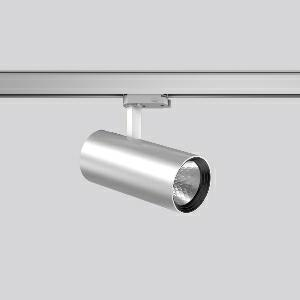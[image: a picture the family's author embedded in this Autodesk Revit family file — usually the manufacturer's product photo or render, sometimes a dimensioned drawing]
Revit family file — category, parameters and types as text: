
# Revit family: deecos_s_mini_742204_004_76_07a7
name_source: partatom
category: Lighting Fixtures
units: mm (PartAtom-declared; Revit-internal decimal feet)

## family parameters
Cut with Voids When Loaded = No
Host = Face
Light Source = No
Part Type = Normal
Room Calculation Point = No
Round Connector Dimension = Use Diameter
Shared = No

## types (1)
- DEECOS S mini (1 x LED Modul 930, 3500 lm, 3000)
    Apparent Load = 29 VA
    Approval mark = CE
    CIE Flux Codes = 99 100 100 100 100
    Color Rendering = 90
    Color Temperature = 3000
    Default Elevation = 1800 mm
    Description = Series: DEECOS S mini
LED surface-mounted projector in modern design with no visible cooling ribs. Housing: die-cast aluminium, powder-coated. Rotation range: 356°. Swivel range: 90°. Black plastic ring and recessed LED to prevent glare from the side. Optical assembly with reflector made of MIRO-Silver with 98% total light reflection for outstanding efficiency - can be changed without tools. Best colour rendering index Ra>90. With adapter for RZB 3-circuit DALI tracks. Suitable for Track on ceiling, Wall track. High quality converter without flickering and stroboscopic effect. The following accessories can be mounted without use of tools: interchangeable lenses, decorative glasses, honeycomb louvre, clear and frosted diffusers, white interchangeable plastic ring. 
Colour: silver
Diameter: 87 mm
Height: 214 mm
Lamp: LED
Socket: without socket
Colour temperature: 3000K
Colour rendering index (CRI): 92
System power: 29 W
Rated luminous flux: 3500 lm
Luminous efficiency: 121 lm/W
Control gear: Converter, dimmable, DALI
Protection class: I
Type of protection: IP 20
    Height = 214 mm
    Lamp = 1 x LED Modul 930
    Lamp Light Flux = 3500 lm
    Lamp count = 1
    Length = 87 mm
    Lifetime = 50000 h
    Luminous efficacy = 121 lm/W
    Manufacturer = RZB
    ModVariant = No
    Model = 742204.004.76
    Mounting Place = Ceiling
    Mounting Type = Rail mounted
    Number of Poles = 1
    OnlyDefault = Yes
    Power Factor = 1
    Product Name = DEECOS S mini
    Product group = Track mounted projectors
    ProductGroupID = 301
    Protection Class = Protection class I
    Protection Degree = IP 20
    RLX_Detail_Level = 1
    RLX_Emergency_Light_Flux = 0 lm
    RLX_Emergency_Type = 0
    RLX_Emergency_Type_DB = No
    RlxData = <blob elided: 37381 chars, md5=155a00f6>
    Socket = socket
    Standby Power = 0 W
    System Light Flux = 3500 lm
    System Power = 29 W
    Type Comments = Product without accessories
    Type Image = 741926.004.jpg
    URL = http://relux.com
    VarID = ---
    Voltage = 230 V
    Voltage Range = 220-240 V
    Weight = 0.00 kg
    Width = 0 mm  [stored 0 ft]

note: [stored X ft] marks values corroborated as IEEE doubles in the binary element streams (Revit-internal decimal feet)

## geometry (parser evidence)
native form markers: Blend x4, Sweep x12
no freeform markers — native parametric forms only
